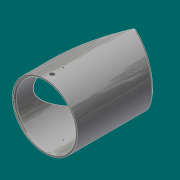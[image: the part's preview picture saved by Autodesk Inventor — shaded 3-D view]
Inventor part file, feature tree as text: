
AUTODESK INVENTOR PART (.ipt)
format: ipt  version: 2017.3 (Build 213257000, 257)  size: 407,040 bytes
history: native  units: in
note: dims shown in document units (in); Inventor stores cm internally (conversion verified against a paired STEP export)
features: other x21, split x9, loft x8, extrude x7, sketch x4, plane x4, hole x2, chamfer x1, pattern_circular x1
ambient origin geometry x8: Origin, YZ Plane, XZ Plane, XY Plane, X Axis, Y Axis, Z Axis, Center Point
bodies: Solid1 (feature_tree)
feature tree (57):
  sketch  "Sketch1"  dims[d0=32.25in d1=35.25in]
  extrude  "Extrusion1"  Depth=35.25in
  sketch  "Sketch2"  dims[d2=48.9921in d3=0.0in d4=22.5deg]
  extrude  "Extrusion2"  TaperAngle=22.5deg  [1 undecoded]
  split  "Split1"
  split  "Split2"
  plane  "Work Plane1"
  plane  "Work Plane2"
  split  "Split3"
  split  "Split4"
  split  "Split5"
  loft  "Loft5"
  loft  "Loft6"
  loft  "Loft7"
  loft  "Loft8"
  loft  "Loft9"
  loft  "Loft10"
  loft  "Loft11"
  plane  "Work Plane3"
  split  "Split6"
  loft  "Loft13"
  chamfer  "Chamfer1"  Angle=90.0deg  [1 undecoded]
  plane  "Work Plane4"
  sketch  "Sketch4"  dims[d5=60.0079in d6=0.0in d7=32.375in]
  hole  "Hole1"  [1 undecoded]
  split  "Split7"
  hole  "Hole2"  [1 undecoded]
  pattern_circular  "Circular Pattern1"  Angle=90.0deg  [1 undecoded]
  sketch  "Sketch5"  dims[d8=0.0in d9=0.0in d10=0.0469in d11=0.0469in d13=1.103in d14=1.103in d15=60.0079in d16=0.0in d18=-1.103in d19=-1.103in d36=0.0in d37=90.0deg d38=0.0in d39=90.0deg d40=0.0in d41=90.0deg d42=0.0in d43=90.0deg d44=0.0in d45=90.0deg d46=0.0in d47=90.0deg d48=0.0in d49=90.0deg d50=0.0in d51=90.0deg d52=0.0in d53=90.0deg d54=0.0in d55=90.0deg d56=0.0in d57=90.0deg d58=0.0in d59=90.0deg d60=0.0in d61=90.0deg d62=0.0in d63=90.0deg d68=0.0in d69=90.0deg d70=0.0in d71=90.0deg d72=0.75in d73=0.125in d74=0.2749in d75=4.0in d76=4.125in d77=2.5625in d78=0.75in d79=0.375in d80=0.25in d81=0.5635in d82=2.0in d83=0.8108in d84=1.0in d85=0.0in d86=6.0in d87=0.891in d88=0.553in d89=0.0246in d90=0.897in d91=0.375in d92=0.25in d93=0.5635in d94=2.0in d95=0.8108in d96=0.7874in d97=360.0deg d99=0.0625in d100=0.0938in d101=75.0deg d102=0.0in d103=0.0in d104=0.0in d105=0.0in]
  split  "Split8"
  split  "Split9"
  other  "Srf1"
  other  "Srf2"
  other  "Edges9"
  other  "Edges10"
  other  "Edges11"
  other  "Edges12"
  other  "Edges13"
  other  "Edges14"
  other  "Edges15"
  other  "Edges16"
  other  "Edges17"
  other  "Edges18"
  other  "Edges19"
  other  "Edges20"
  other  "Edges21"
  other  "Edges22"
  other  "Edges25"
  other  "Edges26"
  other  "Srf3"
  other  "Srf4"
  other  "Srf5"
  extrude  "ExtrusionSrf1"  TaperAngle=0.0deg  [1 undecoded]
  extrude  "ExtrusionSrf2"  TaperAngle=0.0deg  [1 undecoded]
  extrude  "ExtrusionSrf3"  TaperAngle=0.0deg  [1 undecoded]
  extrude  "ExtrusionSrf4"  TaperAngle=0.0deg  [1 undecoded]
  extrude  "ExtrusionSrf5"  TaperAngle=0.0deg  [1 undecoded]
note: 10 required parameter values undecoded (feature->parameter linkage not recoverable at this tier; creation-order binding heuristic only, values carry confidence <= 0.55)
